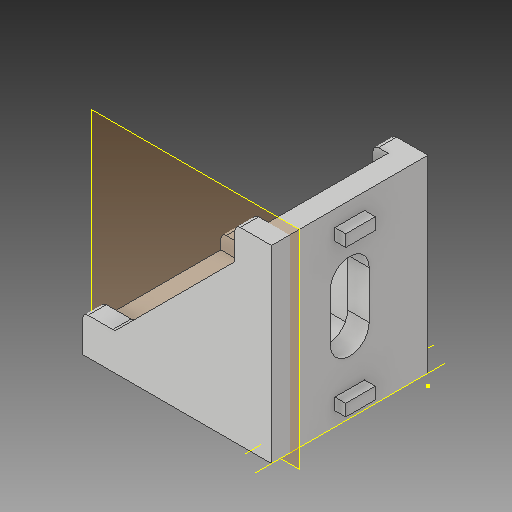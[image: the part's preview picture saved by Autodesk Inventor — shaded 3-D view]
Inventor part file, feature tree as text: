
AUTODESK INVENTOR PART (.ipt)
format: ipt  version: 2018 (Build 220112000, 112)  size: 185,344 bytes
history: native  units: mm
features: sketch x8, other x5, plane x1
ambient origin geometry x8: Origin, YZ Plane, XZ Plane, XY Plane, X Axis, Y Axis, Z Axis, Center Point
bodies: Solid1 (feature_tree)
feature tree (14):
  other  "30mm Bracket_CPY_MIR2_MIR1_MIR.ipt"
  other  "Solid1::30mm Bracket_CPY_MIR2_MIR1_MIR.ipt"
  other  "TaggingFeature1"
  sketch  "Sketch1"  dims[d0=10.0mm]
  sketch  "Sketch2"
  sketch  "Sketch3"
  sketch  "Sketch4"
  sketch  "Sketch5"
  sketch  "Sketch7"
  sketch  "Sketch9"
  sketch  "Sketch10"
  plane  "Work Plane1"
  other  "Work Axis1"
  other  "Work Axis2"
